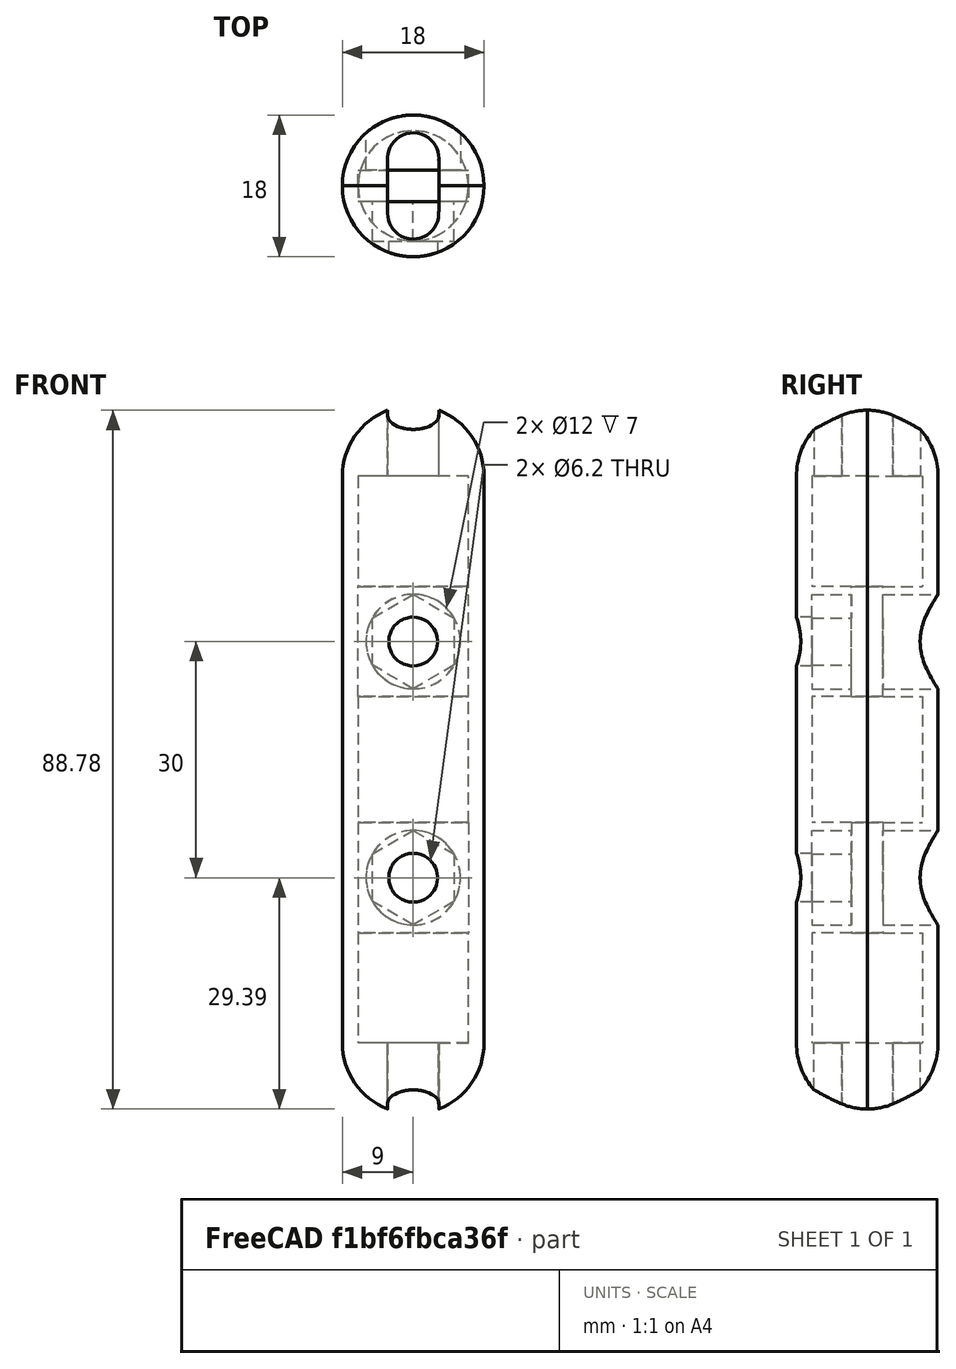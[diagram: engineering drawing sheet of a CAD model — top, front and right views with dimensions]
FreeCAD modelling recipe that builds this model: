
FCSTD DOCUMENT  (FreeCAD 0.21R33771 (Git))
Label: FUSE-Strip-30mm
License: All rights reserved
LicenseURL: https://en.wikipedia.org/wiki/All_rights_reserved
objects: Part::Cut×24, Part::Cylinder×14, Part::Box×8, Part::Mirroring×6, Part::MultiFuse×4, Part::Fuse×4, PartDesign::AdditivePrism×4, PartDesign::Body×4, Part::Sphere×2
note: 74 computed .brp shape members not serialized (recipe doc carries the construction recipe); baked Part::Feature solids carry a one-line shape summary decoded from their .brp

FEATURE [Part::Box] Box004  label="Cube004"
  AttacherType = Attacher::AttachEngine3D
  Height = 18
  Length = 18
  Placement = pos=(-9,0,-9) rot=(0,0,1;0rad)
  Width = 9
FEATURE [Part::Box] Box005  label="Cube005"
  AttacherType = Attacher::AttachEngine3D
  Height = 9
  Length = 18
  Placement = pos=(-9,-9,-9) rot=(0,0,1;0rad)
  Width = 9
FEATURE [Part::Box] Box006  label="Cube006"
  AttacherType = Attacher::AttachEngine3D
  Height = 10
  Length = 6.5
  Placement = pos=(-3.25,-3.25,36) rot=(0,0,1;0rad)
  Width = 6.5
FEATURE [Part::Box] Box007  label="Поглиблення під клему"
  AttacherType = Attacher::AttachEngine3D
  Height = 14
  Length = 14
  Placement = pos=(-7,0,8) rot=(0,0,1;0rad)
  Width = 2
FEATURE [Part::Cylinder] Cylinder007
  Angle = 180
  AttacherType = Attacher::AttachEngine3D
  FirstAngle = 0
  Height = 72
  Placement = pos=(0,0,-36) rot=(0,0,1;0rad)
  Radius = 9
  SecondAngle = 0
FEATURE [Part::Cylinder] Cylinder008  label="Отвір болта 003"
  Angle = 360
  AttacherType = Attacher::AttachEngine3D
  FirstAngle = 0
  Height = 9
  Placement = pos=(0,9,15) rot=(1,0,0;1.5708rad)
  Radius = 3.1
  SecondAngle = 0
FEATURE [Part::Cylinder] Cylinder009  label="Отвір болта 004"
  Angle = 360
  AttacherType = Attacher::AttachEngine3D
  FirstAngle = 0
  Height = 9
  Placement = pos=(0,9,-15) rot=(1,0,0;1.5708rad)
  Radius = 3.1
  SecondAngle = 0
FEATURE [Part::Cylinder] Cylinder010
  Angle = 360
  AttacherType = Attacher::AttachEngine3D
  FirstAngle = 0
  Height = 16
  Placement = pos=(0,0,-8) rot=(0,0,1;0rad)
  Radius = 7
  SecondAngle = 0
FEATURE [Part::Cylinder] Cylinder011
  Angle = 360
  AttacherType = Attacher::AttachEngine3D
  FirstAngle = 0
  Height = 14
  Placement = pos=(0,0,-36) rot=(0,0,1;0rad)
  Radius = 7
  SecondAngle = 0
FEATURE [Part::Cylinder] Cylinder012
  Angle = 360
  AttacherType = Attacher::AttachEngine3D
  FirstAngle = 0
  Height = 14
  Placement = pos=(0,0,22) rot=(0,0,1;0rad)
  Radius = 7
  SecondAngle = 0
FEATURE [Part::Cylinder] Cylinder013
  Angle = 360
  AttacherType = Attacher::AttachEngine3D
  FirstAngle = 0
  Height = 10
  Placement = pos=(0,3.5,36) rot=(0,0,1;0rad)
  Radius = 3.25
  SecondAngle = 0
FEATURE [Part::MultiFuse] Fusion004
  Shapes = -> [Box005,Box004]
FEATURE [Part::Fuse] Fusion007  label="Проріз під провід"
  Base = -> Cylinder013
  Tool = -> Box006
FEATURE [Part::Mirroring] Part__Mirroring004  label="Fusion003 (Mirror #2)001"
  Base = (0,0,0)
  Normal = (0,0,1)
  Source = -> Fusion007
FEATURE [Part::Mirroring] Part__Mirroring005  label="Cube003 (Mirror #3)001"
  Base = (0,0,0)
  Normal = (0,0,1)
  Source = -> Box007
FEATURE [PartDesign::AdditivePrism] Prism002  label="Шляпка болта 003"
  AttacherType = Attacher::AttachEngine3D
  Circumradius = 6
  FirstAngle = 0
  Height = 6
  Polygon = 6
  SecondAngle = 0
FEATURE [PartDesign::Body] Body002
  Group = -> [Prism002]
  Origin = -> Origin002
  Placement = pos=(0,7,-15) rot=(0.935113,-0.250563,0.250563;1.63783rad)
  Tip = -> Prism002
FEATURE [PartDesign::AdditivePrism] Prism003  label="Шляпка болта 004"
  AttacherType = Attacher::AttachEngine3D
  Circumradius = 6
  FirstAngle = 0
  Height = 6
  Polygon = 6
  SecondAngle = 0
FEATURE [PartDesign::Body] Body003
  Group = -> [Prism003]
  Origin = -> Origin003
  Placement = pos=(0,7,15) rot=(0.935113,-0.250563,0.250563;1.63783rad)
  Tip = -> Prism003
FEATURE [Part::Sphere] Sphere001
  Angle1 = -90
  Angle2 = 90
  Angle3 = 360
  AttacherType = Attacher::AttachEngine3D
  Radius = 9
FEATURE [Part::Cut] Cut012
  Base = -> Sphere001
  Placement = pos=(0,0,36) rot=(0,0,1;3.14159rad)
  Tool = -> Fusion004
FEATURE [Part::Mirroring] Part__Mirroring003  label="Cut (Mirror #1)001"
  Base = (0,0,0)
  Normal = (0,0,1)
  Source = -> Cut012
FEATURE [Part::MultiFuse] Fusion005  label="Лодочка001"
  Shapes = -> [Cylinder007,Part__Mirroring003]
FEATURE [Part::Cut] Cut013
  Base = -> Fusion005
  Tool = -> Cylinder008
FEATURE [Part::Cut] Cut014
  Base = -> Cut013
  Tool = -> Cylinder009
FEATURE [Part::Cut] Cut015
  Base = -> Cut014
  Tool = -> Body002
FEATURE [Part::Cut] Cut016
  Base = -> Cut015
  Tool = -> Body003
FEATURE [Part::Cut] Cut017
  Base = -> Cut016
  Tool = -> Cylinder010
FEATURE [Part::Cut] Cut018
  Base = -> Cut017
  Tool = -> Cylinder011
FEATURE [Part::Cut] Cut019
  Base = -> Cut018
  Tool = -> Cylinder012
FEATURE [Part::Fuse] Fusion006
  Base = -> Cut012
  Tool = -> Cut019
FEATURE [Part::Cut] Cut020
  Base = -> Fusion006
  Tool = -> Fusion007
FEATURE [Part::Cut] Cut021
  Base = -> Cut020
  Tool = -> Part__Mirroring004
FEATURE [Part::Cut] Cut022
  Base = -> Cut021
  Tool = -> Box007
FEATURE [Part::Cut] Cut023  label="top"
  Base = -> Cut022
  Placement = pos=(0,0,0) rot=(0,0,1;3.14159rad)
  Tool = -> Part__Mirroring005
FEATURE [Part::Box] Box008  label="Cube007"
  AttacherType = Attacher::AttachEngine3D
  Height = 18
  Length = 18
  Placement = pos=(-9,0,-9) rot=(0,0,1;0rad)
  Width = 9
FEATURE [Part::Box] Box009  label="Cube008"
  AttacherType = Attacher::AttachEngine3D
  Height = 9
  Length = 18
  Placement = pos=(-9,-9,-9) rot=(0,0,1;0rad)
  Width = 9
FEATURE [Part::Box] Box010  label="Cube009"
  AttacherType = Attacher::AttachEngine3D
  Height = 10
  Length = 6.5
  Placement = pos=(-3.25,-3.25,36) rot=(0,0,1;0rad)
  Width = 6.5
FEATURE [Part::Box] Box011  label="Поглиблення під клему001"
  AttacherType = Attacher::AttachEngine3D
  Height = 14
  Length = 14
  Placement = pos=(-7,0,8) rot=(0,0,1;0rad)
  Width = 2
FEATURE [Part::Cylinder] Cylinder014
  Angle = 180
  AttacherType = Attacher::AttachEngine3D
  FirstAngle = 0
  Height = 72
  Placement = pos=(0,0,-36) rot=(0,0,1;0rad)
  Radius = 9
  SecondAngle = 0
FEATURE [Part::Cylinder] Cylinder015  label="Отвір болта 005"
  Angle = 360
  AttacherType = Attacher::AttachEngine3D
  FirstAngle = 0
  Height = 9
  Placement = pos=(0,9,15) rot=(1,0,0;1.5708rad)
  Radius = 6
  SecondAngle = 0
FEATURE [Part::Cylinder] Cylinder016  label="Отвір болта 006"
  Angle = 360
  AttacherType = Attacher::AttachEngine3D
  FirstAngle = 0
  Height = 9
  Placement = pos=(0,9,-15) rot=(1,0,0;1.5708rad)
  Radius = 6
  SecondAngle = 0
FEATURE [Part::Cylinder] Cylinder017
  Angle = 360
  AttacherType = Attacher::AttachEngine3D
  FirstAngle = 0
  Height = 16
  Placement = pos=(0,0,-8) rot=(0,0,1;0rad)
  Radius = 7
  SecondAngle = 0
FEATURE [Part::Cylinder] Cylinder018
  Angle = 360
  AttacherType = Attacher::AttachEngine3D
  FirstAngle = 0
  Height = 14
  Placement = pos=(0,0,-36) rot=(0,0,1;0rad)
  Radius = 7
  SecondAngle = 0
FEATURE [Part::Cylinder] Cylinder019
  Angle = 360
  AttacherType = Attacher::AttachEngine3D
  FirstAngle = 0
  Height = 14
  Placement = pos=(0,0,22) rot=(0,0,1;0rad)
  Radius = 7
  SecondAngle = 0
FEATURE [Part::Cylinder] Cylinder020
  Angle = 360
  AttacherType = Attacher::AttachEngine3D
  FirstAngle = 0
  Height = 10
  Placement = pos=(0,3.5,36) rot=(0,0,1;0rad)
  Radius = 3.25
  SecondAngle = 0
FEATURE [Part::MultiFuse] Fusion008
  Shapes = -> [Box009,Box008]
FEATURE [Part::Fuse] Fusion011  label="Проріз під провід001"
  Base = -> Cylinder020
  Tool = -> Box010
FEATURE [Part::Mirroring] Part__Mirroring007  label="Fusion003 (Mirror #2)002"
  Base = (0,0,0)
  Normal = (0,0,1)
  Source = -> Fusion011
FEATURE [Part::Mirroring] Part__Mirroring008  label="Cube003 (Mirror #3)002"
  Base = (0,0,0)
  Normal = (0,0,1)
  Source = -> Box011
FEATURE [PartDesign::AdditivePrism] Prism005  label="Шляпка болта 006"
  AttacherType = Attacher::AttachEngine3D
  Circumradius = 6
  FirstAngle = 0
  Height = 6
  Polygon = 6
  SecondAngle = 0
FEATURE [PartDesign::Body] Body005
  Group = -> [Prism005]
  Origin = -> Origin005
  Placement = pos=(0,7,15) rot=(0.935113,-0.250563,0.250563;1.63783rad)
  Tip = -> Prism005
FEATURE [Part::Sphere] Sphere002
  Angle1 = -90
  Angle2 = 90
  Angle3 = 360
  AttacherType = Attacher::AttachEngine3D
  Radius = 9
FEATURE [Part::Cut] Cut024
  Base = -> Sphere002
  Placement = pos=(0,0,36) rot=(0,0,1;3.14159rad)
  Tool = -> Fusion008
FEATURE [Part::Mirroring] Part__Mirroring006  label="Cut (Mirror #1)002"
  Base = (0,0,0)
  Normal = (0,0,1)
  Source = -> Cut024
FEATURE [Part::MultiFuse] Fusion009  label="Лодочка002"
  Shapes = -> [Cylinder014,Part__Mirroring006]
FEATURE [Part::Cut] Cut025
  Base = -> Fusion009
  Tool = -> Cylinder015
FEATURE [Part::Cut] Cut026
  Base = -> Cut025
  Tool = -> Cylinder016
FEATURE [PartDesign::AdditivePrism] Prism004  label="Шляпка болта 005"
  AttacherType = Attacher::AttachEngine3D
  Circumradius = 6
  FirstAngle = 0
  Height = 6
  Polygon = 6
  SecondAngle = 0
FEATURE [PartDesign::Body] Body004
  Group = -> [Prism004]
  Origin = -> Origin004
  Placement = pos=(0,7,-15) rot=(0.935113,-0.250563,0.250563;1.63783rad)
  Tip = -> Prism004
FEATURE [Part::Cut] Cut027
  Base = -> Cut026
  Tool = -> Body004
FEATURE [Part::Cut] Cut028
  Base = -> Cut027
  Tool = -> Body005
FEATURE [Part::Cut] Cut029
  Base = -> Cut028
  Tool = -> Cylinder017
FEATURE [Part::Cut] Cut030
  Base = -> Cut029
  Tool = -> Cylinder018
FEATURE [Part::Cut] Cut031
  Base = -> Cut030
  Tool = -> Cylinder019
FEATURE [Part::Fuse] Fusion010
  Base = -> Cut024
  Tool = -> Cut031
FEATURE [Part::Cut] Cut032
  Base = -> Fusion010
  Tool = -> Fusion011
FEATURE [Part::Cut] Cut033
  Base = -> Cut032
  Tool = -> Part__Mirroring007
FEATURE [Part::Cut] Cut034
  Base = -> Cut033
  Tool = -> Box011
FEATURE [Part::Cut] Cut035  label="bottom"
  Base = -> Cut034
  Tool = -> Part__Mirroring008
